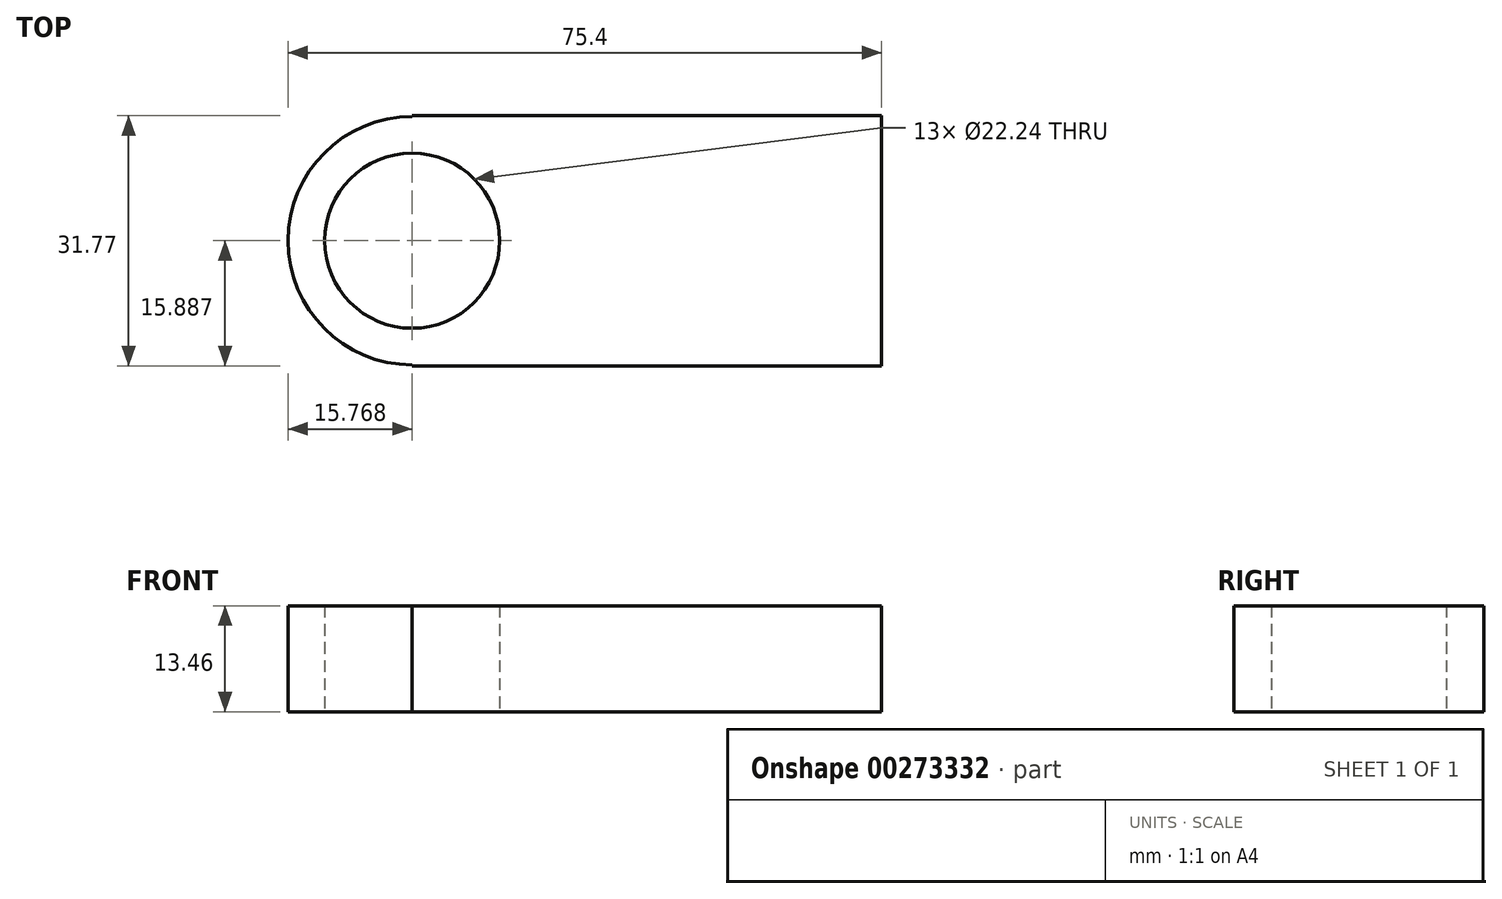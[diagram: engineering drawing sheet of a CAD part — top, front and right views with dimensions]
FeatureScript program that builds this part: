
annotation { "Feature Type Name" : "Feature", "Feature Type Description" : "" }
export const myFeature = defineFeature(function(context is Context, id is Id, definition is map)
    precondition{}
    {
        {
            var Q0;
            Q0=qCreatedBy(makeId("Top.planeOp"),FACE);
            var sketch = newSketch(context, id + "F0", { "sketchPlane" : qUnion([Q0])});
            skLineSegment(sketch, "E0.bottom", {"start": v(0, 0) * mm, "end": v(-59.63, 0) * mm});
            skLineSegment(sketch, "E0.top", {"start": v(0, 31.77) * mm, "end": v(-59.63, 31.77) * mm});
            skLineSegment(sketch, "E0.left", {"start": v(0, 0) * mm, "end": v(0, 31.77) * mm});
            skLineSegment(sketch, "E0.right", {"start": v(-59.63, 0) * mm, "end": v(-59.63, 31.77) * mm});
            skCircle(sketch, "E1", {"center": v(-59.63, 15.89) * mm, "radius": 15.77 * mm});
            skCircle(sketch, "E2", {"center": v(-59.63, 15.89) * mm, "radius": 11.12 * mm});
            skSolve(sketch);
        }
        {
            var Q0;
            {var subQ0=sQuery(id+"F0.wireOp",EDGE,"E1");var subQ1=sQuery(id+"F0.wireOp",EDGE,"E0.right");var subQ2=makeQuery(id+"F0.imprint","INTERSECT",VERTEX,{"disambiguationData":[OD(0.0)],"derivedFrom":[subQ1,subQ0]});Q0=makeQuery(id+"F0.imprint","IMPRINT",FACE,{"disambiguationData":[TD([[makeQuery(id+"F0.imprint","IMPRINT",EDGE,{"disambiguationData":[TD([[subQ2,-1.0]])],"derivedFrom":subQ1}),1.0]])]});}
            var Q1;
            {var subQ0=sQuery(id+"F0.wireOp",EDGE,"E1");var subQ1=sQuery(id+"F0.wireOp",EDGE,"E0.right");var subQ2=makeQuery(id+"F0.imprint","INTERSECT",VERTEX,{"disambiguationData":[OD(0.0)],"derivedFrom":[subQ1,subQ0]});Q1=makeQuery(id+"F0.imprint","IMPRINT",FACE,{"disambiguationData":[TD([[makeQuery(id+"F0.imprint","IMPRINT",EDGE,{"disambiguationData":[TD([[subQ2,-1.0]])],"derivedFrom":subQ1}),-1.0]])]});}
            var Q2;
            {var subQ1=sQuery(id+"F0.wireOp",EDGE,"E0.bottom");Q2=makeQuery(id+"F0.imprint","IMPRINT",FACE,{"disambiguationData":[TD([[makeQuery(id+"F0.imprint","IMPRINT",EDGE,{"derivedFrom":subQ1}),-1.0]])]});}
            extrude(context, id + "F1", {"entities" : qUnion([Q0, Q1, Q2]), "depth" : 13.46 * mm});
        }
    });
